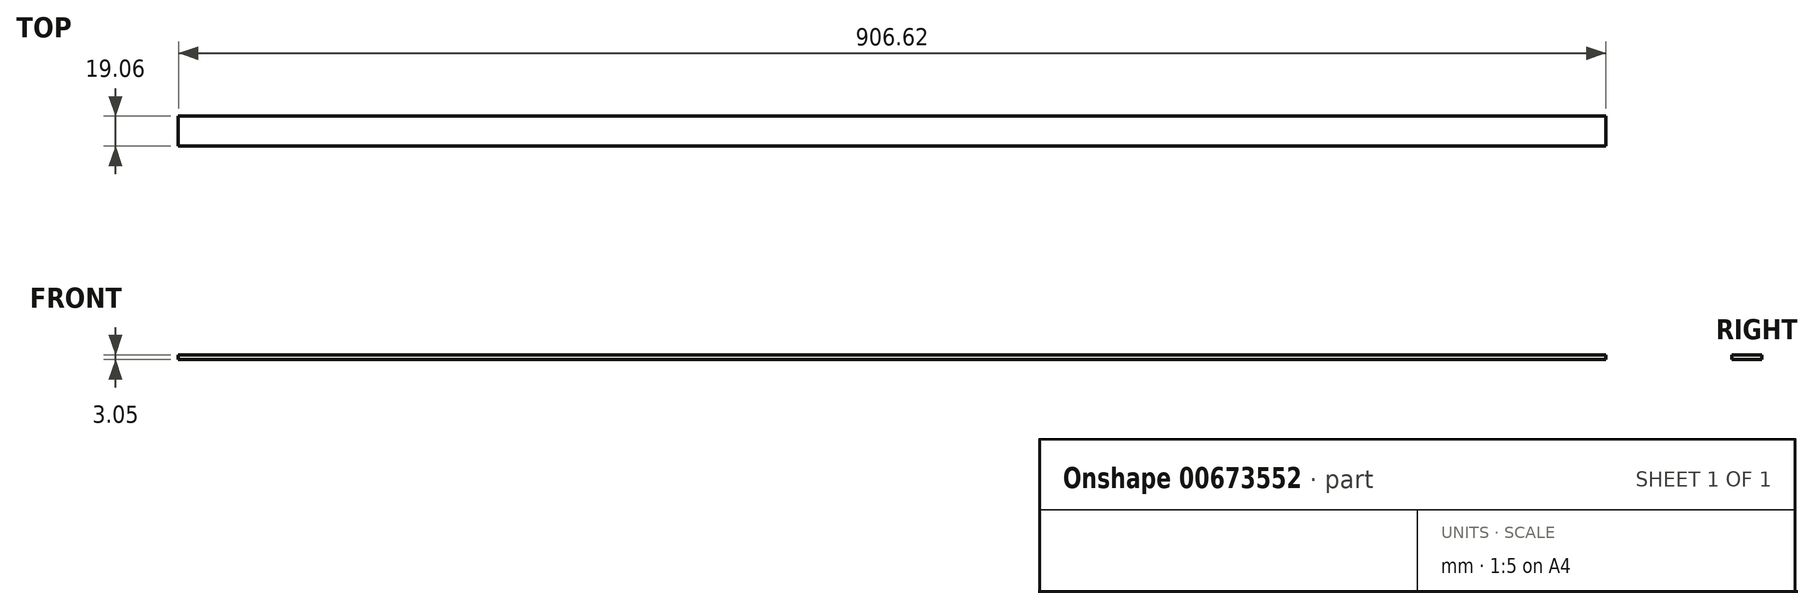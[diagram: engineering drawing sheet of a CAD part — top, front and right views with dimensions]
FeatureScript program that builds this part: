
annotation { "Feature Type Name" : "Feature", "Feature Type Description" : "" }
export const myFeature = defineFeature(function(context is Context, id is Id, definition is map)
    precondition{}
    {
        {
            var Q0;
            Q0=qCreatedBy(makeId("Right.planeOp"),FACE);
            var sketch = newSketch(context, id + "F0", { "sketchPlane" : qUnion([Q0])});
            skLineSegment(sketch, "E0.bottom", {"start": v(-9.52, 3.05) * mm, "end": v(9.52, 3.05) * mm});
            skLineSegment(sketch, "E0.top", {"start": v(-9.53, 0) * mm, "end": v(9.53, 0) * mm});
            skLineSegment(sketch, "E0.left", {"start": v(-9.53, 3.05) * mm, "end": v(-9.53, 0) * mm});
            skLineSegment(sketch, "E0.right", {"start": v(9.52, 3.05) * mm, "end": v(9.52, 0) * mm});
            skSolve(sketch);
        }
        {
            var Q0;
            Q0=qSketchRegion(id+"F0",true);
            extrude(context, id + "F1", {"entities" : qUnion([Q0]), "endBound" : BoundingType.SYMMETRIC, "depth" : 906.63 * mm, "offsetDistance" : 25.4 * mm});
        }
    });
